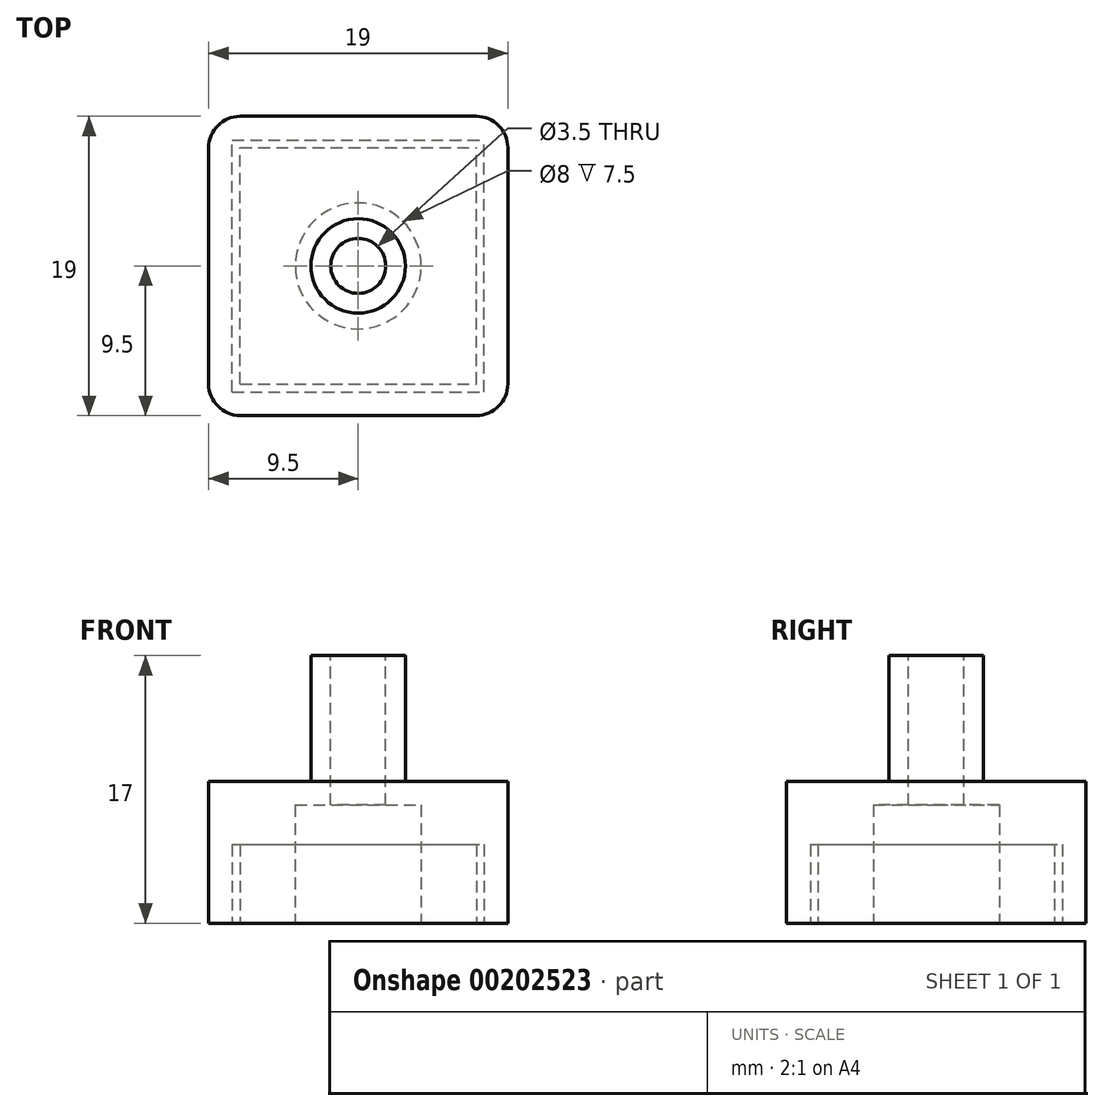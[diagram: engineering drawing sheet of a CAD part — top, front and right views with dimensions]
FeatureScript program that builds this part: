
annotation { "Feature Type Name" : "Feature", "Feature Type Description" : "" }
export const myFeature = defineFeature(function(context is Context, id is Id, definition is map)
    precondition{}
    {
        {
            var Q0;
            Q0=qCreatedBy(makeId("Front.planeOp"),FACE);
            var sketch = newSketch(context, id + "F0", { "sketchPlane" : qUnion([Q0])});
            skLineSegment(sketch, "E0", {"start": v(0, 0) * mm, "end": v(9.5, 0) * mm});
            skLineSegment(sketch, "E1", {"start": v(9.5, 0) * mm, "end": v(9.5, 9) * mm});
            skLineSegment(sketch, "E2", {"start": v(9.5, 9) * mm, "end": v(-9.5, 9) * mm});
            skLineSegment(sketch, "E3", {"start": v(-9.5, 9) * mm, "end": v(-9.5, 0) * mm});
            skLineSegment(sketch, "E4", {"start": v(-9.5, 0) * mm, "end": v(0, 0) * mm});
            skSolve(sketch);
        }
        {
            var Q0;
            Q0 = qSketchRegion(id + "F0", true);
            extrude(context, id + "F1", {"entities" : qUnion([Q0]), "depth" : 19 * mm, "symmetric" : true});
        }
        {
            var Q0;
            Q0=makeQuery(id+"F1.opExtrude","SWEPT_FACE",FACE,{"disambiguationData":[OSD([sQuery(id+"F0.wireOp",EDGE,"E2")])]});
            var sketch = newSketch(context, id + "F2", { "sketchPlane" : qUnion([Q0])});
            skCircle(sketch, "E5", {"center": v(0, 0) * mm, "radius": 3 * mm});
            skSolve(sketch);
        }
        {
            var Q0;
            Q0 = qSketchRegion(id + "F2", true);
            extrude(context, id + "F3", {"entities" : qUnion([Q0]), "operationType" : NewBodyOperationType.ADD, "depth" : 8 * mm});
        }
        {
            var Q0;
            Q0=makeQuery(id+"F3.opExtrude","CAP_FACE",FACE,{"disambiguationData":[OSD([sQuery(id+"F2.wireOp",EDGE,"E5")])],"isStart":false});
            var sketch = newSketch(context, id + "F4", { "sketchPlane" : qUnion([Q0])});
            skCircle(sketch, "E6", {"center": v(0, 0) * mm, "radius": 1.75 * mm});
            skSolve(sketch);
        }
        {
            var Q0;
            Q0 = qSketchRegion(id + "F4", true);
            extrude(context, id + "F5", {"entities" : qUnion([Q0]), "operationType" : NewBodyOperationType.REMOVE, "oppositeDirection" : true, "depth" : 17 * mm});
        }
        {
            var Q0;
            Q0=makeQuery(id+"F1.opExtrude","SWEPT_FACE",FACE,{"disambiguationData":[OSD([sQuery(id+"F0.wireOp",EDGE,"E0"),sQuery(id+"F0.wireOp",EDGE,"E4")])]});
            var sketch = newSketch(context, id + "F6", { "sketchPlane" : qUnion([Q0])});
            skLineSegment(sketch, "E7.bottom", {"start": v(-8, 8) * mm, "end": v(8, 8) * mm});
            skLineSegment(sketch, "E7.top", {"start": v(-8, -8) * mm, "end": v(8, -8) * mm});
            skLineSegment(sketch, "E7.left", {"start": v(-8, 8) * mm, "end": v(-8, -8) * mm});
            skLineSegment(sketch, "E7.right", {"start": v(8, 8) * mm, "end": v(8, -8) * mm});
            skPoint(sketch, "E7.middle", {"position": v(0, 0) * mm});
            skLineSegment(sketch, "E8.bottom", {"start": v(-7.5, 7.5) * mm, "end": v(7.5, 7.5) * mm});
            skLineSegment(sketch, "E8.top", {"start": v(-7.5, -7.5) * mm, "end": v(7.5, -7.5) * mm});
            skLineSegment(sketch, "E8.left", {"start": v(-7.5, 7.5) * mm, "end": v(-7.5, -7.5) * mm});
            skLineSegment(sketch, "E8.right", {"start": v(7.5, 7.5) * mm, "end": v(7.5, -7.5) * mm});
            skSolve(sketch);
        }
        {
            var Q0;
            Q0=makeQuery(id+"F6.imprint","IMPRINT",FACE,{"disambiguationData":[TD([[makeQuery(id+"F6.imprint","IMPRINT",EDGE,{"derivedFrom":sQuery(id+"F6.wireOp",EDGE,"E7.bottom")}),-1.0]])]});
            extrude(context, id + "F7", {"entities" : qUnion([Q0]), "operationType" : NewBodyOperationType.REMOVE, "oppositeDirection" : true, "depth" : 5 * mm});
        }
        {
            var Q0;
            Q0=makeQuery(id+"F1.opExtrude","CAP_EDGE",EDGE,{"disambiguationData":[OSD([sQuery(id+"F0.wireOp",EDGE,"E3")])],"isStart":false});
            var Q1;
            Q1=makeQuery(id+"F1.opExtrude","CAP_EDGE",EDGE,{"disambiguationData":[OSD([sQuery(id+"F0.wireOp",EDGE,"E1")])],"isStart":false});
            var Q2;
            Q2=makeQuery(id+"F1.opExtrude","CAP_EDGE",EDGE,{"disambiguationData":[OSD([sQuery(id+"F0.wireOp",EDGE,"E3")])],"isStart":true});
            var Q3;
            Q3=makeQuery(id+"F1.opExtrude","CAP_EDGE",EDGE,{"disambiguationData":[OSD([sQuery(id+"F0.wireOp",EDGE,"E1")])],"isStart":true});
            fillet(context, id + "F8", {"entities" : qUnion([Q0, Q1, Q2, Q3]), "radius" : 2 * mm, "tangentPropagation" : true, "allowEdgeOverflow" : false});
        }
        {
            var Q0;
            Q0=makeQuery(id+"F7.boolean.opBoolean","SPLIT",FACE,{"disambiguationData":[TD([makeQuery(id+"F5.boolean.opBoolean","COPY",FACE,{"derivedFrom":makeQuery(id+"F5.opExtrude","SWEPT_FACE",FACE,{"disambiguationData":[OSD([sQuery(id+"F4.wireOp",EDGE,"E6")])]})})])],"derivedFrom":makeQuery(id+"F1.opExtrude","SWEPT_FACE",FACE,{"disambiguationData":[OSD([sQuery(id+"F0.wireOp",EDGE,"E0"),sQuery(id+"F0.wireOp",EDGE,"E4")])]})});
            var sketch = newSketch(context, id + "F9", { "sketchPlane" : qUnion([Q0])});
            skCircle(sketch, "E9", {"center": v(0, 0) * mm, "radius": 4 * mm});
            skSolve(sketch);
        }
        {
            var Q0;
            Q0=makeQuery(id+"F9.imprint","IMPRINT",FACE,{"disambiguationData":[TD([[makeQuery(id+"F9.imprint","IMPRINT",EDGE,{"derivedFrom":sQuery(id+"F9.wireOp",EDGE,"E9")}),1.0]])]});
            extrude(context, id + "F10", {"entities" : qUnion([Q0]), "operationType" : NewBodyOperationType.REMOVE, "oppositeDirection" : true, "depth" : 7.5 * mm});
        }
    });
